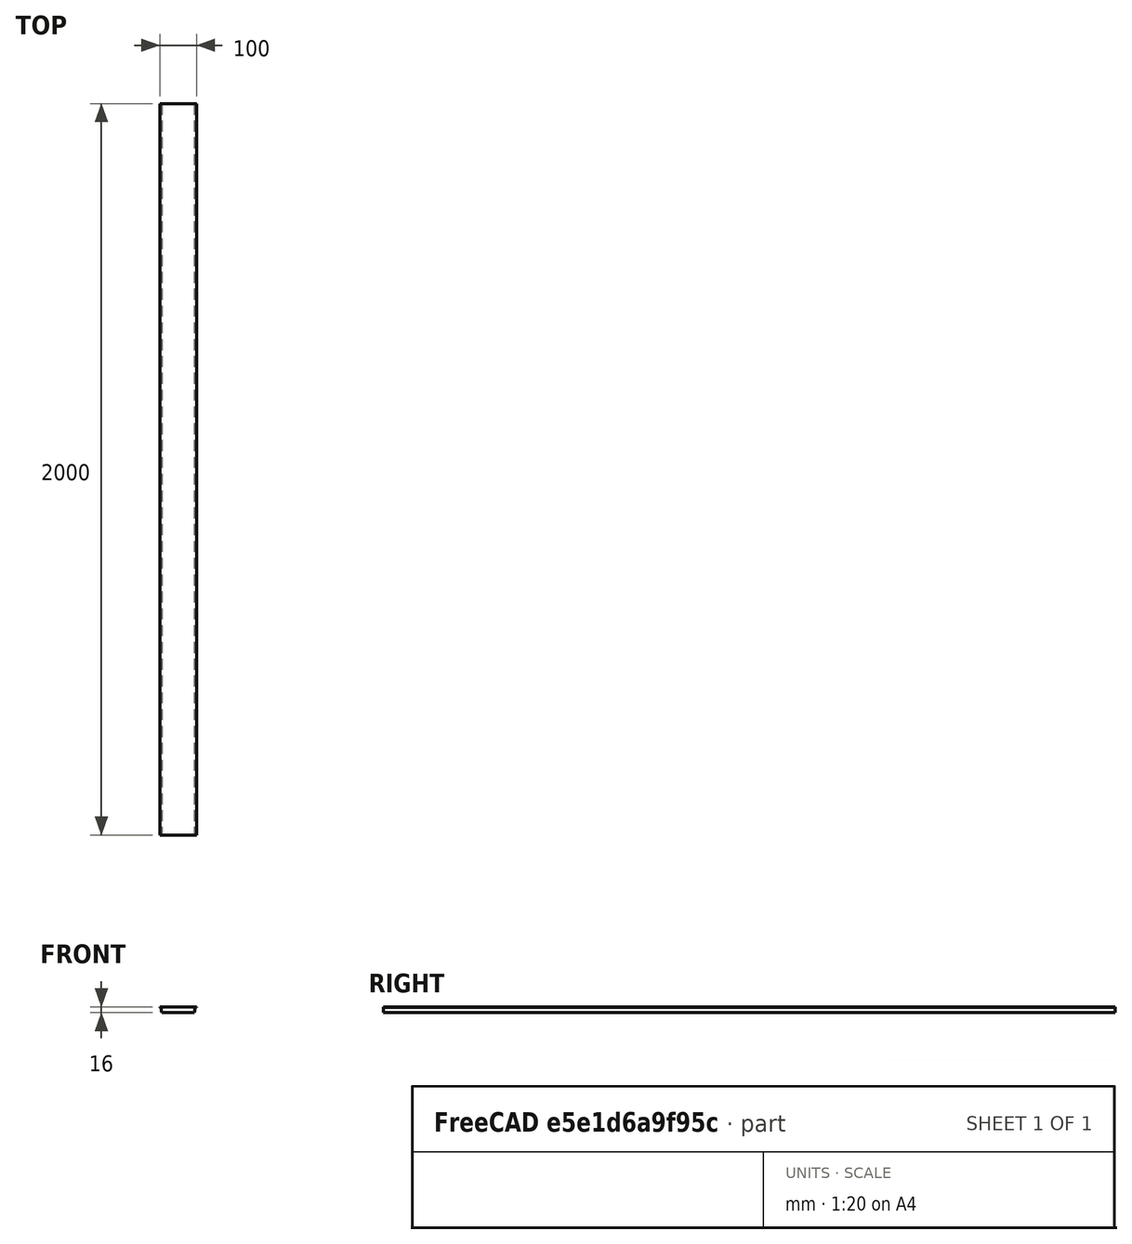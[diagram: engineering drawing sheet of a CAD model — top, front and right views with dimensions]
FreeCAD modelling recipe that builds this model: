
FCSTD DOCUMENT  (FreeCAD 0.15R4671 (Git))
Label: Plaque_alveolaire_old
License: All rights reserved
LicenseURL: http://en.wikipedia.org/wiki/All_rights_reserved
objects: Sketcher::SketchObject×1, PartDesign::Pad×1
note: 3 computed .brp shape members not serialized (recipe doc carries the construction recipe); baked Part::Feature solids carry a one-line shape summary decoded from their .brp

FEATURE [Sketcher::SketchObject] Sketch
  Placement = pos=(0,0,0) rot=(1,0,0;1.5708rad)
  sketch-geometry (8):
    g0: LineSegment StartX=-50 StartY=0 StartZ=0 EndX=50 EndY=0 EndZ=0
    g1: LineSegment StartX=50 StartY=0 StartZ=0 EndX=50 EndY=-2 EndZ=0
    g2: LineSegment StartX=50 StartY=-2 StartZ=0 EndX=47 EndY=-2 EndZ=0
    g3: LineSegment StartX=47 StartY=-2 StartZ=0 EndX=44 EndY=-16 EndZ=0
    g4: LineSegment StartX=44 StartY=-16 StartZ=0 EndX=-44 EndY=-16 EndZ=0
    g5: LineSegment StartX=-44 StartY=-16 StartZ=0 EndX=-47 EndY=-2 EndZ=0
    g6: LineSegment StartX=-47 StartY=-2 StartZ=0 EndX=-50 EndY=-2 EndZ=0
    g7: LineSegment StartX=-50 StartY=-2 StartZ=0 EndX=-50 EndY=0 EndZ=0
  constraints (24):
    c: PointOnObject(g0,g-1)
    c: Horizontal(g0)
    c: Coincident(g0,g1)
    c: Vertical(g1)
    c: Coincident(g1,g2)
    c: Horizontal(g2)
    c: Coincident(g2,g3)
    c: Coincident(g3,g4)
    c: Horizontal(g4)
    c: Coincident(g4,g5)
    c: Coincident(g5,g6)
    c: Horizontal(g6)
    c: Coincident(g6,g7)
    c: Coincident(g7,g0)
    c: Vertical(g7)
    c: DistanceY(g0,g6) = -2
    c: DistanceX(g6,g5) = 3
    c: DistanceX(g0,g0) = 100
    c: Symmetric(g0,g0,g-2)
    c: Symmetric(g6,g1,g-2)
    c: Symmetric(g5,g2,g-2)
    c: Symmetric(g4,g3,g-2)
    c: DistanceX(g4,g3) = 88
    c: DistanceY(g0,g4) = -16
FEATURE [PartDesign::Pad] Pad
  Length = 2000
  Length2 = 100
  Midplane = true
  Placement = pos=(0,0,0) rot=(1,0,0;1.5708rad)
  Sketch = -> Sketch
  Type = 0
